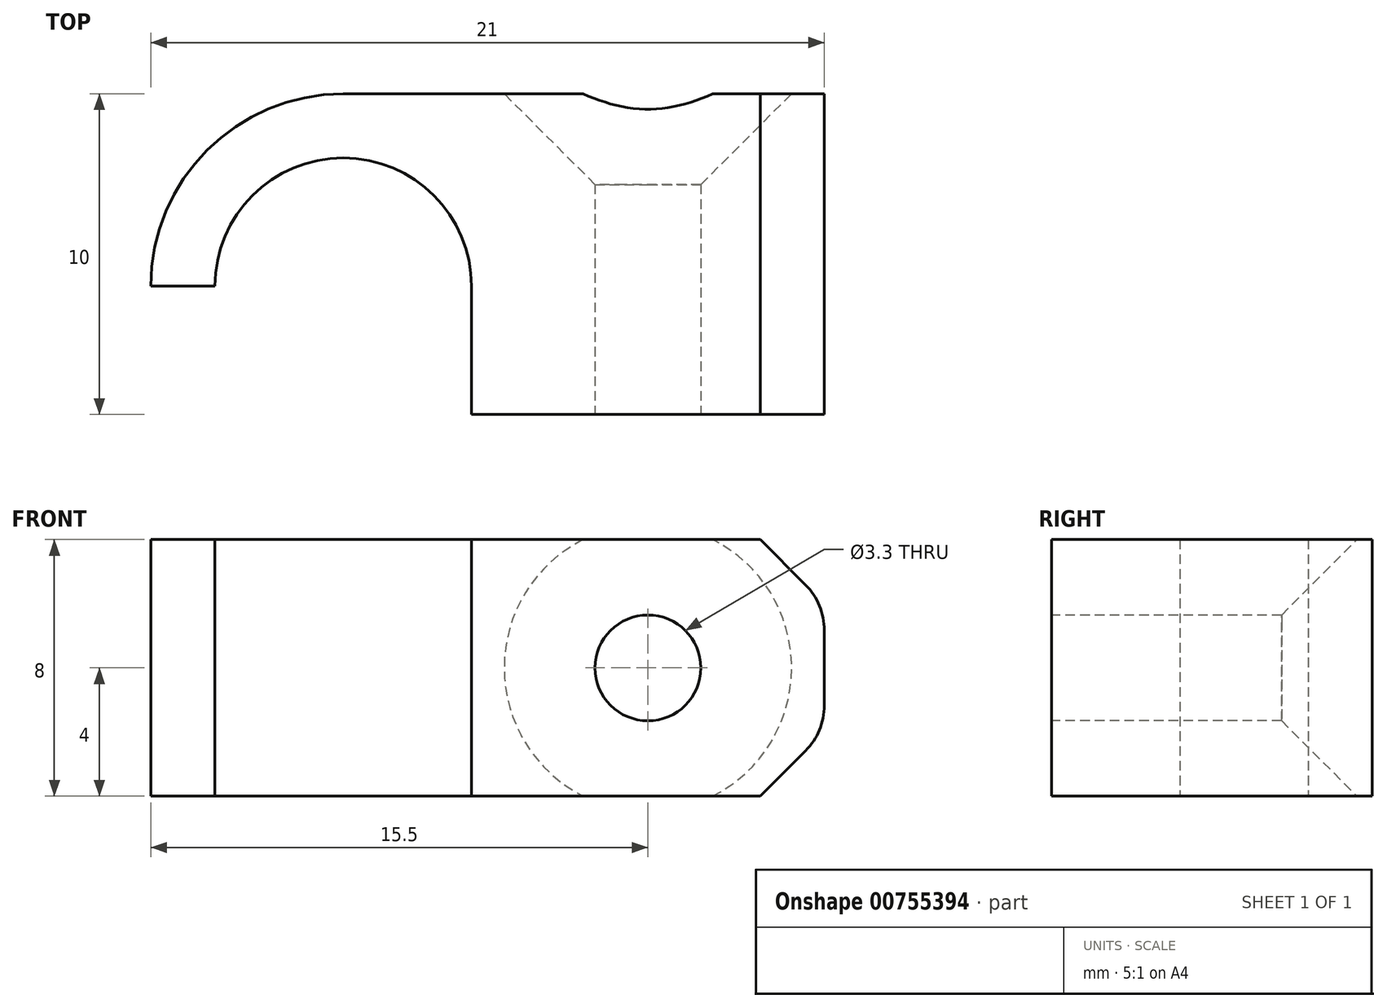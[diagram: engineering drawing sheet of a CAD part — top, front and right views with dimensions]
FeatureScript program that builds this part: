
annotation { "Feature Type Name" : "Feature", "Feature Type Description" : "" }
export const myFeature = defineFeature(function(context is Context, id is Id, definition is map)
    precondition{}
    {
        {
            var Q0;
            Q0=qCreatedBy(makeId("Top.planeOp"),FACE);
            var sketch = newSketch(context, id + "F0", { "sketchPlane" : qUnion([Q0])});
            skArc(sketch, "E0", {"start": v(4, 0) * mm, "mid": v(0, 4) * mm, "end": v(-4, 0) * mm});
            skArc(sketch, "E1.0", {"start": v(0, 6) * mm, "mid": v(-4.24, 4.24) * mm, "end": v(-6, 0) * mm});
            skLineSegment(sketch, "E2", {"start": v(0, 6) * mm, "end": v(15, 6) * mm});
            skLineSegment(sketch, "E3", {"start": v(15, 6) * mm, "end": v(15, -4) * mm});
            skLineSegment(sketch, "E4", {"start": v(4, -4) * mm, "end": v(15, -4) * mm});
            skLineSegment(sketch, "E5", {"start": v(-6, 0) * mm, "end": v(-4, 0) * mm});
            skLineSegment(sketch, "E6", {"start": v(4, 0) * mm, "end": v(4, -4) * mm});
            skPoint(sketch, "E7.orphan", {"position": v(0, -4) * mm});
            skSolve(sketch);
        }
        {
            var Q0;
            Q0=makeQuery(id+"F0.imprint","IMPRINT",FACE,{"disambiguationData":[TD([[makeQuery(id+"F0.imprint","IMPRINT",EDGE,{"derivedFrom":sQuery(id+"F0.wireOp",EDGE,"E0")}),-1.0]])]});
            extrude(context, id + "F1", {"entities" : qUnion([Q0]), "depth" : 8 * mm, "offsetDistance" : 25 * mm, "symmetric" : true});
        }
        {
            var Q0;
            Q0=makeQuery(id+"F1.opExtrude","SWEPT_FACE",FACE,{"disambiguationData":[OSD([sQuery(id+"F0.wireOp",EDGE,"E2")])]});
            var sketch = newSketch(context, id + "F2", { "sketchPlane" : qUnion([Q0])});
            skLineSegment(sketch, "E8", {"start": v(-15, 4) * mm, "end": v(-4, -4) * mm, "construction": true});
            skPoint(sketch, "E9", {"position": v(-9.5, 0) * mm});
            skSolve(sketch);
        }
        {
            var Q0;
            Q0=sQuery(id+"F2.wireOp",VERTEX,"E9");
            var Q1;
            Q1=makeQuery(id+"F1.opExtrude","SWEPT_BODY",BODY,{"disambiguationData":[OSD([sQuery(id+"F0.wireOp",EDGE,"E0"),sQuery(id+"F0.wireOp",EDGE,"E1.0"),sQuery(id+"F0.wireOp",EDGE,"E2"),sQuery(id+"F0.wireOp",EDGE,"E3"),sQuery(id+"F0.wireOp",EDGE,"E4"),sQuery(id+"F0.wireOp",EDGE,"E5"),sQuery(id+"F0.wireOp",EDGE,"E6")])]});
            hole(context, id + "F3", {"style" : HoleStyle.C_SINK, "endStyle" : HoleEndStyle.THROUGH, "standardTappedOrClearance" : lookupTablePath({ "standard" : "ISO", "engagement" : "75%", "pitch" : "0.7 mm", "size" : "M4", "type" : "Tapped" }), "standardBlindInLast" : lookupTablePath({ "standard" : "ISO", "engagement" : "75%", "pitch" : "0.7 mm", "size" : "M4", "type" : "Tapped" }), "holeDiameter" : 3.3 * mm, "cSinkDiameter" : 8.96 * mm, "cSinkAngle" : 90 * degree, "majorDiameter" : 4 * mm, "showTappedDepth" : true, "isTappedThrough" : true, "tappedDepth" : 12 * mm, "tapClearance" : 3, "locations" : qUnion([Q0]), "scope" : qUnion([Q1])});
        }
        {
            var Q0;
            Q0=makeQuery(id+"F1.opExtrude","CAP_EDGE",EDGE,{"disambiguationData":[OSD([sQuery(id+"F0.wireOp",EDGE,"E3")])],"isStart":true});
            var Q1;
            Q1=makeQuery(id+"F1.opExtrude","CAP_EDGE",EDGE,{"disambiguationData":[OSD([sQuery(id+"F0.wireOp",EDGE,"E3")])],"isStart":false});
            chamfer(context, id + "F4", {"entities" : qUnion([Q0, Q1]), "width" : 2 * mm, "tangentPropagation" : true});
        }
        {
            var Q0;
            {var subQ0=sQuery(id+"F0.wireOp",EDGE,"E3");Q0=makeQuery(id+"F4.opChamfer","BLEND_EDGE",EDGE,{"blendedFrom":[makeQuery(id+"F1.opExtrude","CAP_EDGE",EDGE,{"disambiguationData":[OSD([subQ0])],"isStart":false}),makeQuery(id+"F1.opExtrude","SWEPT_FACE",FACE,{"disambiguationData":[OSD([subQ0])]})],"blendedInto":[makeQuery(id+"F1.opExtrude","SWEPT_FACE",FACE,{"disambiguationData":[OSD([subQ0])]})]});}
            var Q1;
            {var subQ0=sQuery(id+"F0.wireOp",EDGE,"E3");Q1=makeQuery(id+"F4.opChamfer","BLEND_EDGE",EDGE,{"blendedFrom":[makeQuery(id+"F1.opExtrude","CAP_EDGE",EDGE,{"disambiguationData":[OSD([subQ0])],"isStart":true}),makeQuery(id+"F1.opExtrude","SWEPT_FACE",FACE,{"disambiguationData":[OSD([subQ0])]})],"blendedInto":[makeQuery(id+"F1.opExtrude","SWEPT_FACE",FACE,{"disambiguationData":[OSD([subQ0])]})]});}
            fillet(context, id + "F5", {"entities" : qUnion([Q0, Q1]), "radius" : 2 * mm, "tangentPropagation" : true, "allowEdgeOverflow" : false});
        }
    });
